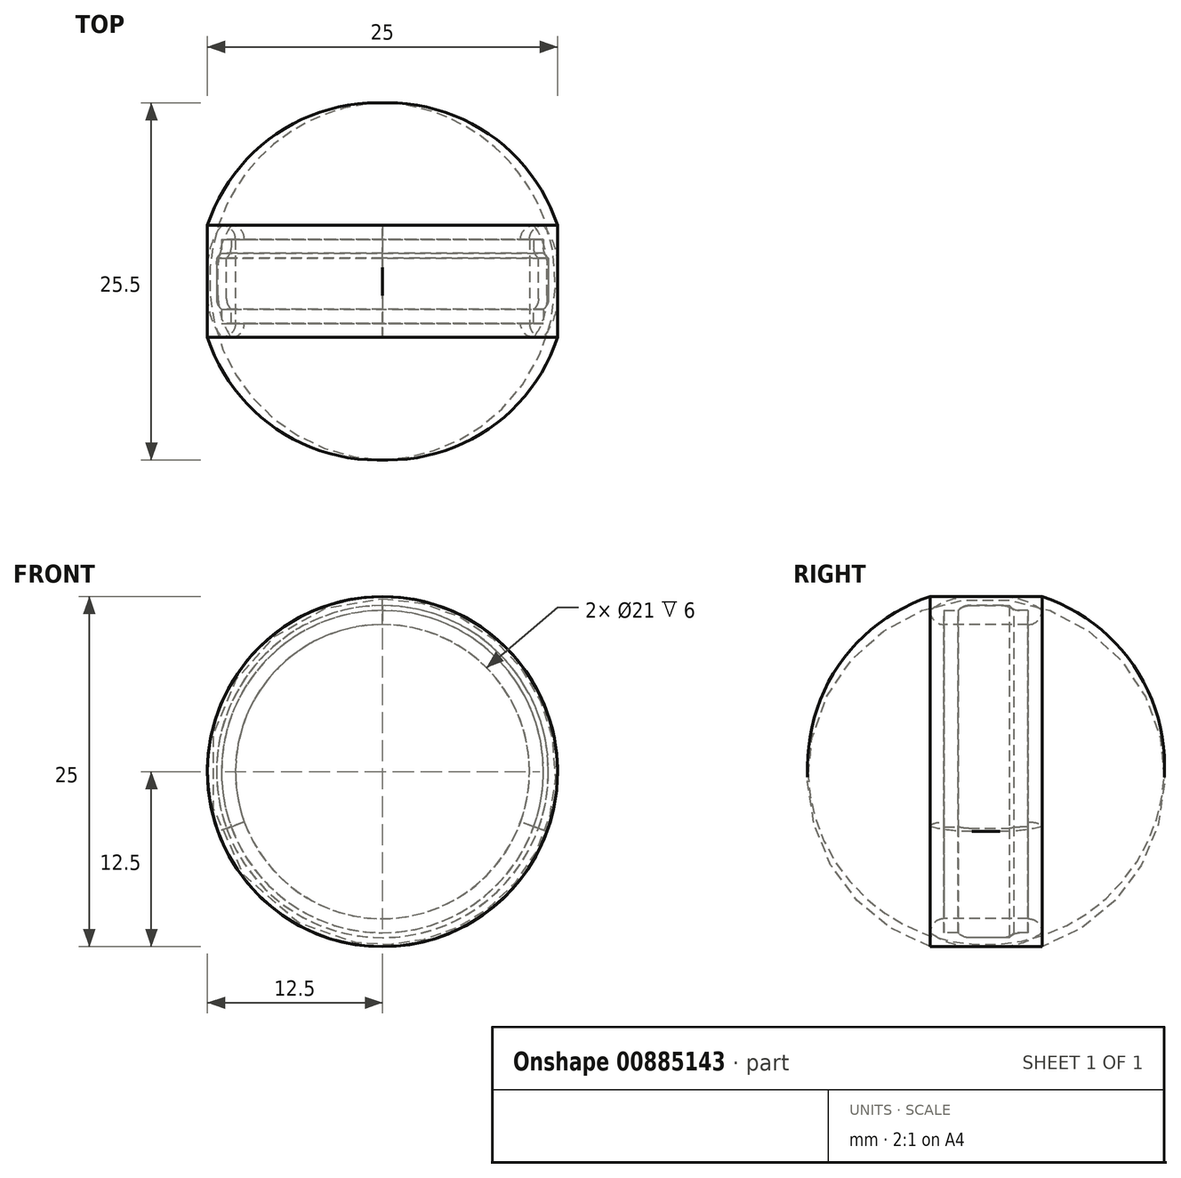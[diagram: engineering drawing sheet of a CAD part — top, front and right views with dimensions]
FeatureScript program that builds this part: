
annotation { "Feature Type Name" : "Feature", "Feature Type Description" : "" }
export const myFeature = defineFeature(function(context is Context, id is Id, definition is map)
    precondition{}
    {
        {
            var Q0;
            Q0=qCreatedBy(makeId("Right.planeOp"),FACE);
            var sketch = newSketch(context, id + "F0", { "sketchPlane" : qUnion([Q0])});
            skLineSegment(sketch, "E0", {"start": v(-19.63, -17.5) * mm, "end": v(80.37, -17.5) * mm, "construction": true});
            skLineSegment(sketch, "E1", {"start": v(-43.65, -17.5) * mm, "end": v(56.35, -17.5) * mm, "construction": true});
            skLineSegment(sketch, "E2.left", {"start": v(17.1, -5) * mm, "end": v(17.1, -7) * mm});
            skLineSegment(sketch, "E2.right", {"start": v(25.1, -5) * mm, "end": v(25.1, -6) * mm});
            skLineSegment(sketch, "E3", {"start": v(18.1, -6) * mm, "end": v(19.1, -6) * mm});
            skLineSegment(sketch, "E4", {"start": v(24.1, -6) * mm, "end": v(23.1, -6) * mm});
            skLineSegment(sketch, "E5", {"start": v(19.1, -6) * mm, "end": v(19.45, -5.65) * mm});
            skLineSegment(sketch, "E6", {"start": v(23.1, -6) * mm, "end": v(22.75, -5.65) * mm});
            skLineSegment(sketch, "E7", {"start": v(19.45, -5.65) * mm, "end": v(22.75, -5.65) * mm});
            skArc(sketch, "E8", {"start": v(25.1, -5) * mm, "mid": v(21.1, -4.36) * mm, "end": v(17.1, -5) * mm});
            skPoint(sketch, "E9", {"position": v(21.1, -5) * mm});
            skLineSegment(sketch, "E10", {"start": v(25.1, -6) * mm, "end": v(25.1, -7) * mm});
            skLineSegment(sketch, "E11", {"start": v(18.1, -6) * mm, "end": v(18.1, -7) * mm});
            skLineSegment(sketch, "E12", {"start": v(24.1, -6) * mm, "end": v(24.1, -7) * mm});
            skLineSegment(sketch, "E13", {"start": v(17.1, -5) * mm, "end": v(25.1, -5) * mm});
            skLineSegment(sketch, "E14", {"start": v(17.1, -7) * mm, "end": v(18.1, -7) * mm});
            skLineSegment(sketch, "E15", {"start": v(24.1, -7) * mm, "end": v(25.1, -7) * mm});
            skLineSegment(sketch, "E16", {"start": v(18.1, -7) * mm, "end": v(24.1, -7) * mm});
            skLineSegment(sketch, "E17.left", {"start": v(30.1, -5) * mm, "end": v(30.1, -7) * mm});
            skLineSegment(sketch, "E17.right", {"start": v(38.1, -5) * mm, "end": v(38.1, -6) * mm});
            skLineSegment(sketch, "E18", {"start": v(31.1, -6) * mm, "end": v(32.1, -6) * mm});
            skLineSegment(sketch, "E19", {"start": v(37.1, -6) * mm, "end": v(36.1, -6) * mm});
            skLineSegment(sketch, "E20", {"start": v(32.1, -6) * mm, "end": v(32.85, -5.25) * mm});
            skLineSegment(sketch, "E21", {"start": v(36.1, -6) * mm, "end": v(35.35, -5.25) * mm});
            skLineSegment(sketch, "E22", {"start": v(32.85, -5.25) * mm, "end": v(35.35, -5.25) * mm});
            skArc(sketch, "E23", {"start": v(38.1, -5) * mm, "mid": v(34.1, -4.36) * mm, "end": v(30.1, -5) * mm});
            skPoint(sketch, "E24", {"position": v(34.1, -5) * mm});
            skLineSegment(sketch, "E25", {"start": v(38.1, -6) * mm, "end": v(38.1, -7) * mm});
            skLineSegment(sketch, "E26", {"start": v(31.1, -6) * mm, "end": v(31.1, -7) * mm});
            skLineSegment(sketch, "E27", {"start": v(37.1, -6) * mm, "end": v(37.1, -7) * mm});
            skLineSegment(sketch, "E28", {"start": v(30.1, -5) * mm, "end": v(38.1, -5) * mm});
            skLineSegment(sketch, "E29", {"start": v(30.1, -7) * mm, "end": v(31.1, -7) * mm});
            skLineSegment(sketch, "E30", {"start": v(37.1, -7) * mm, "end": v(38.1, -7) * mm});
            skLineSegment(sketch, "E31", {"start": v(31.1, -7) * mm, "end": v(37.1, -7) * mm});
            skSolve(sketch);
        }
        {
            var Q0;
            Q0=makeQuery(id+"F0.imprint","IMPRINT",FACE,{"disambiguationData":[TD([[makeQuery(id+"F0.imprint","IMPRINT",EDGE,{"derivedFrom":sQuery(id+"F0.wireOp",EDGE,"E3")}),-1.0]])]});
            var Q1;
            Q1=sQuery(id+"F0.wireOp",EDGE,"E0");
            revolve(context, id + "F1", {"surfaceOperationType" : NewSurfaceOperationType.NEW, "entities" : qUnion([Q0]), "axis" : qUnion([Q1]), "revolveType" : RevolveType.FULL});
        }
        {
            var Q0;
            Q0=makeQuery(id+"F1.opRevolve","SWEPT_EDGE",EDGE,{"disambiguationData":[OSD([sQuery(id+"F0.wireOp",EDGE,"E5"),sQuery(id+"F0.wireOp",EDGE,"E7")])]});
            var Q1;
            Q1=makeQuery(id+"F1.opRevolve","SWEPT_EDGE",EDGE,{"disambiguationData":[OSD([sQuery(id+"F0.wireOp",EDGE,"E6"),sQuery(id+"F0.wireOp",EDGE,"E7")])]});
            fillet(context, id + "F2", {"entities" : qUnion([Q0, Q1]), "radius" : 1 * mm, "tangentPropagation" : true, "allowEdgeOverflow" : false});
        }
        {
            var Q0;
            Q0=makeQuery(id+"F0.imprint","IMPRINT",FACE,{"disambiguationData":[TD([[makeQuery(id+"F0.imprint","IMPRINT",EDGE,{"derivedFrom":sQuery(id+"F0.wireOp",EDGE,"E2.left")}),1.0]])]});
            var Q1;
            Q1=sQuery(id+"F0.wireOp",EDGE,"E0");
            revolve(context, id + "F3", {"surfaceOperationType" : NewSurfaceOperationType.NEW, "entities" : qUnion([Q0]), "axis" : qUnion([Q1]), "revolveType" : RevolveType.ONE_DIRECTION, "angle" : 110 * degree});
        }
        {
            var Q0;
            Q0=makeQuery(id+"F3.opRevolve","SWEPT_EDGE",EDGE,{"disambiguationData":[OSD([sQuery(id+"F0.wireOp",EDGE,"E4"),sQuery(id+"F0.wireOp",EDGE,"E6")])]});
            var Q1;
            Q1=makeQuery(id+"F3.opRevolve","SWEPT_EDGE",EDGE,{"disambiguationData":[OSD([sQuery(id+"F0.wireOp",EDGE,"E5"),sQuery(id+"F0.wireOp",EDGE,"E7")])]});
            var Q2;
            Q2=makeQuery(id+"F3.opRevolve","SWEPT_EDGE",EDGE,{"disambiguationData":[OSD([sQuery(id+"F0.wireOp",EDGE,"E2.left"),sQuery(id+"F0.wireOp",EDGE,"E14")])]});
            var Q3;
            Q3=makeQuery(id+"F3.opRevolve","SWEPT_EDGE",EDGE,{"disambiguationData":[OSD([sQuery(id+"F0.wireOp",EDGE,"E10"),sQuery(id+"F0.wireOp",EDGE,"E15")])]});
            fillet(context, id + "F4", {"entities" : qUnion([Q0, Q1, Q2, Q3]), "radius" : 1 * mm, "tangentPropagation" : true, "allowEdgeOverflow" : false});
        }
        {
            var Q0;
            Q0=makeQuery(id+"F0.imprint","IMPRINT",FACE,{"disambiguationData":[TD([[makeQuery(id+"F0.imprint","IMPRINT",EDGE,{"derivedFrom":sQuery(id+"F0.wireOp",EDGE,"E2.left")}),1.0]])]});
            var Q1;
            Q1=sQuery(id+"F0.wireOp",EDGE,"E0");
            revolve(context, id + "F5", {"surfaceOperationType" : NewSurfaceOperationType.NEW, "entities" : qUnion([Q0]), "axis" : qUnion([Q1]), "revolveType" : RevolveType.TWO_DIRECTIONS, "angle" : 250 * degree, "angleBack" : 110 * degree});
        }
        {
            var Q0;
            Q0=makeQuery(id+"F5.opRevolve","SWEPT_EDGE",EDGE,{"disambiguationData":[OSD([sQuery(id+"F0.wireOp",EDGE,"E4"),sQuery(id+"F0.wireOp",EDGE,"E6")])]});
            var Q1;
            Q1=makeQuery(id+"F5.opRevolve","SWEPT_EDGE",EDGE,{"disambiguationData":[OSD([sQuery(id+"F0.wireOp",EDGE,"E10"),sQuery(id+"F0.wireOp",EDGE,"E15")])]});
            var Q2;
            Q2=makeQuery(id+"F5.opRevolve","SWEPT_EDGE",EDGE,{"disambiguationData":[OSD([sQuery(id+"F0.wireOp",EDGE,"E2.left"),sQuery(id+"F0.wireOp",EDGE,"E14")])]});
            var Q3;
            Q3=makeQuery(id+"F5.opRevolve","SWEPT_EDGE",EDGE,{"disambiguationData":[OSD([sQuery(id+"F0.wireOp",EDGE,"E5"),sQuery(id+"F0.wireOp",EDGE,"E7")])]});
            fillet(context, id + "F6", {"entities" : qUnion([Q0, Q1, Q2, Q3]), "radius" : 1 * mm, "tangentPropagation" : true, "allowEdgeOverflow" : false});
        }
        {
            var Q0;
            Q0=makeQuery(id+"F0.imprint","IMPRINT",FACE,{"disambiguationData":[TD([[makeQuery(id+"F0.imprint","IMPRINT",EDGE,{"derivedFrom":sQuery(id+"F0.wireOp",EDGE,"E2.left")}),1.0]])]});
            var Q1;
            Q1=sQuery(id+"F0.wireOp",EDGE,"E0");
            revolve(context, id + "F7", {"surfaceOperationType" : NewSurfaceOperationType.NEW, "entities" : qUnion([Q0]), "axis" : qUnion([Q1]), "revolveType" : RevolveType.TWO_DIRECTIONS, "angle" : 360 * degree, "angleBack" : 250 * degree});
        }
        {
            var Q0;
            Q0=makeQuery(id+"F7.opRevolve","SWEPT_EDGE",EDGE,{"disambiguationData":[OSD([sQuery(id+"F0.wireOp",EDGE,"E5"),sQuery(id+"F0.wireOp",EDGE,"E7")])]});
            var Q1;
            Q1=makeQuery(id+"F7.opRevolve","SWEPT_EDGE",EDGE,{"disambiguationData":[OSD([sQuery(id+"F0.wireOp",EDGE,"E2.left"),sQuery(id+"F0.wireOp",EDGE,"E14")])]});
            var Q2;
            Q2=makeQuery(id+"F7.opRevolve","SWEPT_EDGE",EDGE,{"disambiguationData":[OSD([sQuery(id+"F0.wireOp",EDGE,"E10"),sQuery(id+"F0.wireOp",EDGE,"E15")])]});
            var Q3;
            Q3=makeQuery(id+"F7.opRevolve","SWEPT_EDGE",EDGE,{"disambiguationData":[OSD([sQuery(id+"F0.wireOp",EDGE,"E4"),sQuery(id+"F0.wireOp",EDGE,"E6")])]});
            fillet(context, id + "F8", {"entities" : qUnion([Q0, Q1, Q2, Q3]), "radius" : 1 * mm, "tangentPropagation" : true, "allowEdgeOverflow" : false});
        }
        {
            var Q0;
            Q0=makeQuery(id+"F0.imprint","IMPRINT",FACE,{"disambiguationData":[TD([[makeQuery(id+"F0.imprint","IMPRINT",EDGE,{"derivedFrom":sQuery(id+"F0.wireOp",EDGE,"E8")}),1.0]])]});
            var Q1;
            Q1=sQuery(id+"F0.wireOp",EDGE,"E1");
            revolve(context, id + "F9", {"surfaceOperationType" : NewSurfaceOperationType.NEW, "entities" : qUnion([Q0]), "axis" : qUnion([Q1]), "revolveType" : RevolveType.FULL});
        }
        {
            var Q0;
            Q0=makeQuery(id+"F5.opRevolve","SWEPT_EDGE",EDGE,{"disambiguationData":[OSD([sQuery(id+"F0.wireOp",EDGE,"E2.right"),sQuery(id+"F0.wireOp",EDGE,"E8"),sQuery(id+"F0.wireOp",EDGE,"E13")])]});
            var Q1;
            Q1=makeQuery(id+"F5.opRevolve","SWEPT_EDGE",EDGE,{"disambiguationData":[OSD([sQuery(id+"F0.wireOp",EDGE,"E2.left"),sQuery(id+"F0.wireOp",EDGE,"E8"),sQuery(id+"F0.wireOp",EDGE,"E13")])]});
            var Q2;
            Q2=makeQuery(id+"F7.opRevolve","SWEPT_EDGE",EDGE,{"disambiguationData":[OSD([sQuery(id+"F0.wireOp",EDGE,"E2.left"),sQuery(id+"F0.wireOp",EDGE,"E8"),sQuery(id+"F0.wireOp",EDGE,"E13")])]});
            var Q3;
            Q3=makeQuery(id+"F7.opRevolve","SWEPT_EDGE",EDGE,{"disambiguationData":[OSD([sQuery(id+"F0.wireOp",EDGE,"E2.right"),sQuery(id+"F0.wireOp",EDGE,"E8"),sQuery(id+"F0.wireOp",EDGE,"E13")])]});
            var Q4;
            Q4=makeQuery(id+"F3.opRevolve","SWEPT_EDGE",EDGE,{"disambiguationData":[OSD([sQuery(id+"F0.wireOp",EDGE,"E2.right"),sQuery(id+"F0.wireOp",EDGE,"E8"),sQuery(id+"F0.wireOp",EDGE,"E13")])]});
            var Q5;
            Q5=makeQuery(id+"F3.opRevolve","SWEPT_EDGE",EDGE,{"disambiguationData":[OSD([sQuery(id+"F0.wireOp",EDGE,"E2.left"),sQuery(id+"F0.wireOp",EDGE,"E8"),sQuery(id+"F0.wireOp",EDGE,"E13")])]});
            fillet(context, id + "F10", {"entities" : qUnion([Q0, Q1, Q2, Q3, Q4, Q5]), "radius" : 5 * mm, "tangentPropagation" : true, "allowEdgeOverflow" : false});
        }
    });
